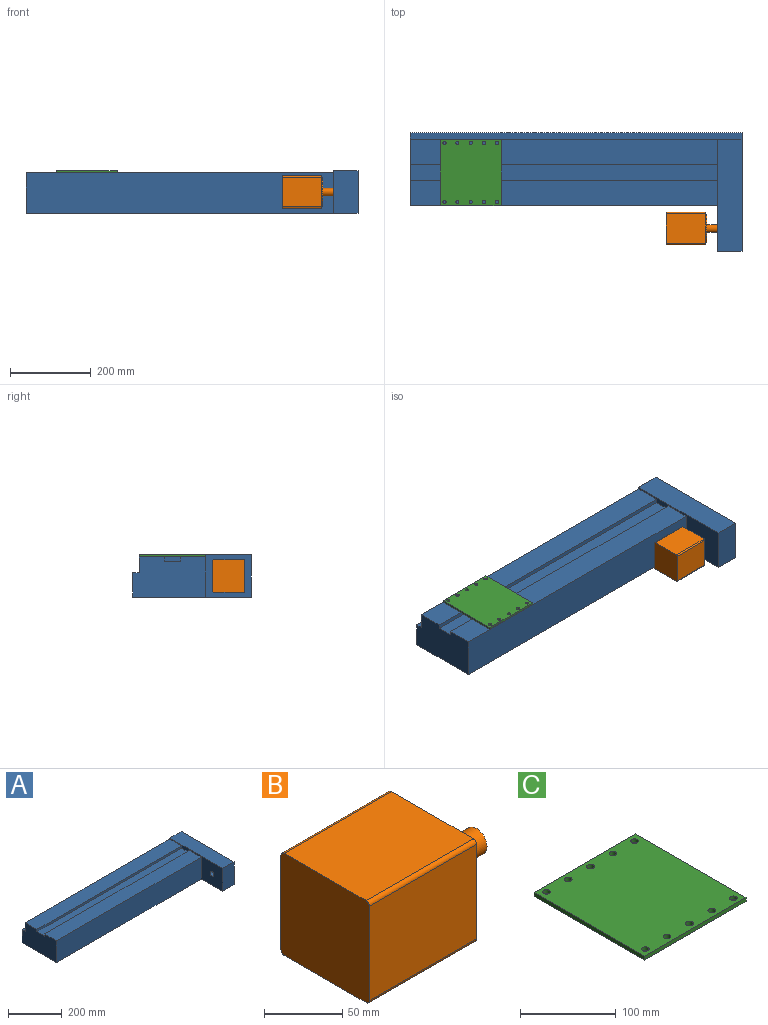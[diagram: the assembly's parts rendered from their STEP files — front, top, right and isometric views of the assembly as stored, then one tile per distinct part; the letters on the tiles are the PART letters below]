
ASSEMBLY  parts=3 mates=2
PART A: 17 faces, bbox 820x293x104 mm
  f0: plane 760x62.5mm, normal (0,0,1), area 47500mm2, adj f1,f6,f10,f12
  f1: plane 181x99mm, normal (-1,0,0), area 16895mm2, adj f0,f2,f3,f4,f5,f6,f11,f12
  f2: plane 760x99mm, normal (0,-1,0), area 75240mm2, adj f1,f3,f10,f11
  f3: plane 820x293mm, normal (0,0,-1), area 155140mm2, adj f1,f2,f4,f8,f9,f10
  f4: plane 820x60mm, normal (0,1,0), area 49200mm2, adj f1,f3,f5,f8
  f5: plane 820x16mm, normal (0,0,1), area 13120mm2, adj f1,f4,f6,f8
  f6: plane 820x44mm, normal (0,1,0), area 32280mm2, adj f0,f1,f5,f7,f8,f10
  f7: plane 277x60mm, normal (0,0,1), area 16620mm2, adj f6,f8,f9,f10
  f8: plane 293x104mm, normal (1,0,0), area 29768mm2, adj f3,f4,f5,f6,f7,f9
  f9: plane 104x60mm, normal (0,-1,0), area 6240mm2, adj f3,f7,f8,f10
  f10: plane 277x104mm, normal (-1,0,0), area 12558.8mm2, adj f0,f2,f3,f6,f7,f9,f11,f12
  f11: plane 760x62.5mm, normal (0,0,1), area 47500mm2, adj f1,f2,f10,f13
  f12: plane 760x10mm, normal (0,-1,0), area 7600mm2, adj f0,f1,f10,f14
  f13: plane 760x10mm, normal (0,1,0), area 7600mm2, adj f1,f10,f11,f14
  f14: plane 760x40mm, normal (0,0,1), area 30400mm2, adj f1,f10,f12,f13
  f15: cylinder r=10mm len=20mm, axis (-1,0,0), area 1256.6mm2, adj f10,f16
  f16: plane 20x20mm, normal (-1,0,0), area 314.2mm2, adj f15
PART B: 22 faces, bbox 137x80x80 mm
  f0: plane 97x74mm, normal (0,0,1), area 7178mm2, adj f4,f5,f10,f13
  f1: plane 97x74mm, normal (0,-1,0), area 7178mm2, adj f4,f5,f10,f11
  f2: plane 97x74mm, normal (0,0,-1), area 7178mm2, adj f4,f5,f11,f12
  f3: plane 97x74mm, normal (0,1,0), area 7178mm2, adj f4,f5,f12,f13
  f4: plane 80x80mm, normal (1,0,0), area 2389.9mm2, adj f0,f1,f2,f3,f6,f10,f11,f12
  f5: plane 80x80mm, normal (-1,0,0), area 6392.3mm2, adj f0,f1,f2,f3,f10,f11,f12,f13
  f6: cylinder r=35mm len=70mm, axis (-1,0,0), area 659.7mm2, adj f4,f7
  f7: plane 70x70mm, normal (1,0,0), area 3564.9mm2, adj f6,f9
  f8: plane 19x19mm, normal (1,0,0), area 283.5mm2, adj f9
  f9: cylinder r=9.5mm len=37mm, axis (-1,0,0), area 2208.5mm2, adj f7,f8
  f10: cylinder r=3mm len=97mm, axis (1,0,0), area 457.1mm2, adj f0,f1,f4,f5
  f11: cylinder r=3mm len=97mm, axis (-1,0,0), area 457.1mm2, adj f1,f2,f4,f5
  f12: cylinder r=3mm len=97mm, axis (1,0,0), area 457.1mm2, adj f2,f3,f4,f5
  f13: cylinder r=3mm len=97mm, axis (-1,0,0), area 457.1mm2, adj f0,f3,f4,f5
  f14: cylinder r=3.5mm len=15mm, axis (1,0,0), area 329.9mm2, adj f4,f15
  f15: plane 7x7mm, normal (1,0,0), area 38.5mm2, adj f14
  f16: cylinder r=3.5mm len=15mm, axis (1,0,0), area 329.9mm2, adj f4,f17
  f17: plane 7x7mm, normal (1,0,0), area 38.5mm2, adj f16
  f18: cylinder r=3.5mm len=15mm, axis (1,0,0), area 329.9mm2, adj f4,f19
  f19: plane 7x7mm, normal (1,0,0), area 38.5mm2, adj f18
  f20: cylinder r=3.5mm len=15mm, axis (1,0,0), area 329.9mm2, adj f4,f21
  f21: plane 7x7mm, normal (1,0,0), area 38.5mm2, adj f20
PART C: 16 faces, bbox 150x163x5 mm
  f0: plane 163x5mm, normal (1,0,0), area 815mm2, adj f1,f3,f4,f5
  f1: plane 150x5mm, normal (0,1,0), area 750mm2, adj f0,f2,f4,f5
  f2: plane 163x5mm, normal (-1,0,0), area 815mm2, adj f1,f3,f4,f5
  f3: plane 150x5mm, normal (0,-1,0), area 750mm2, adj f0,f2,f4,f5
  f4: plane 163x150mm, normal (0,0,1), area 23947.3mm2, adj f0,f1,f2,f3,f6,f7,f8,f9
  f5: plane 163x150mm, normal (0,0,-1), area 23947.3mm2, adj f0,f1,f2,f3,f6,f7,f8,f9
  f6: cylinder r=4mm len=8mm, axis (0,0,1), area 125.7mm2, adj f4,f5
  f7: cylinder r=4mm len=8mm, axis (0,0,1), area 125.7mm2, adj f4,f5
  f8: cylinder r=4mm len=8mm, axis (0,0,1), area 125.7mm2, adj f4,f5
  f9: cylinder r=4mm len=8mm, axis (0,0,1), area 125.7mm2, adj f4,f5
  f10: cylinder r=4mm len=8mm, axis (0,0,1), area 125.7mm2, adj f4,f5
  f11: cylinder r=4mm len=8mm, axis (0,0,1), area 125.7mm2, adj f4,f5
  f12: cylinder r=4mm len=8mm, axis (0,0,1), area 125.7mm2, adj f4,f5
  f13: cylinder r=4mm len=8mm, axis (0,0,1), area 125.7mm2, adj f4,f5
  f14: cylinder r=4mm len=8mm, axis (0,0,1), area 125.7mm2, adj f4,f5
  f15: cylinder r=4mm len=8mm, axis (0,0,1), area 125.7mm2, adj f4,f5
PLACE A rot(axis=(-1,0,0),0deg) t=(-52.31,44.68,87.13)mm fixed
PLACE B rot(axis=(-1,0,0),0deg) t=(-239.31,60.68,75.13)mm
PLACE C t=(-52.31,44.68,87.13)mm
MATE fastened B.f6 <-> A.f15  axis (1,0,0) through (-102.31,-93.82,139.13)mm
MATE slider C.f2 <-> A.f1  axis (-1,0,0) through (-797.31,44.68,186.13)mm
